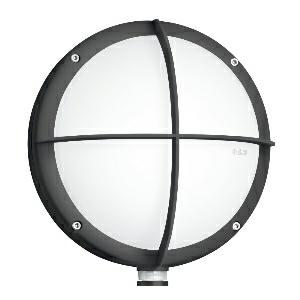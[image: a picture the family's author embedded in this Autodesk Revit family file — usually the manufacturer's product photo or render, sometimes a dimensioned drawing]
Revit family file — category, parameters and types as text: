
# Revit family: l_331_led_053093
name_source: partatom
category: Leuchten
revit_build: Autodesk Revit 2016 (Build: 20190508_0715(x64)
units: mm (PartAtom-declared; Revit-internal decimal feet)

## family parameters
Basisbauteil = Fläche
Beim Laden mit Abzugskörper schneiden = Nein
Bemaßung runder Anschluss = Durchmesser verwenden
Gemeinsam genutzt = Nein
Lichtquelle = Nein
Raumberechnungspunkt = Nein
Teiletyp = Normal

## types (1)
- L 331 LED (1 x , 720 lm, 3000 K)
    Beschreibung = Dimensions (L x W x H): 124 x 253 x 270 mm; Mains power supply: 220 – 240 V / 50 – 60 Hz; Mounting height max.: 2,50 m; Sensor Technology: passive infrared; Output: 9 W; Interconnection: Yes; Type of interconnection: Master/master; Slave modeselectable: No; Luminous flux: 720 lm; Colour temperature: 3000 K; Colour variation LED: SDCM3; Colour Rendering Index CRI: 80-89; With lamp: Yes, STEINEL LED system; Lamp: LED cannot be replaced; LED life expectancy (max. °C): 50000 h; Base: without; LED cooling system: Passive Thermo Control; With motion detector: Yes; Detection angle: 360 °; Sneak-by guard: Yes; Capability of masking out individual segments: Yes; Electronic scalability: No; Mechanical scalability: No; Reach, radial: r = 2 m (13 m²); Reach, tangential: r = 7 m (154 m²); Photo-cell controller: Yes; Twilight setting: 2 – 1000 lx; Time setting: 5 sec – 15 min; Basic light level function: Yes; Basic light level function time: 10/30 min, all night; Functions: 4 programme settings geared to practical needs, can be selected on removable sensor module; Soft light start: Yes; Continuous light: selectable, 4h; Impact resistance: IK10; IP-rating: IP44; Protection class: II; Ambient temperature: -10 – 50 °C; Housing material: Plastic; Cover material: Plastic, opal; Manufacturer's Warranty: 5 years; Settings via: Potentiometers; Cover material: shrouds; Version: Anthracite; PU1, EAN: 4007841053093
    Color Rendering = 80-89
    Color Temperature = 3000 K
    Frequency = 50 Hz, 60 Hz
    Height = 270 mm
    Hersteller = Steinel
    Lamp Light Flux = 720 lm
    Lamp count = 1
    Lampe = 1 x
    Length = 124 mm
    Luminous efficacy = 0 lm/W
    ModVariant = Nein
    Modell = 053093
    Mounting Type = Surface mounted
    Number of Poles = 1
    OnlyDefault = Ja
    Power Factor = 1
    Product Name = L 331 LED
    Product group = Sensor-switched indoor light
    ProductGroupID = 30
    Protection Class = Protection class II
    Protection Degree = IP 34
    RlxData = <blob elided: 47689 chars, md5=324017a3>
    Scheinlast = 9 VA
    Socket = socket
    Standby Power = 0 W
    System Light Flux = 0 lm
    System Power = 9 W
    Typenbild = produkt1_053093.jpg
    Typenkommentare = Product without accessories
    URL = http://relux.com
    VarID = ---
    Voltage = 0 V
    Vorgabe-Ansicht = 1800 mm
    Weight = 0.00 kg
    Width = 253 mm

## geometry (parser evidence)
native form markers: Blend x4, Sweep x11
no freeform markers — native parametric forms only
